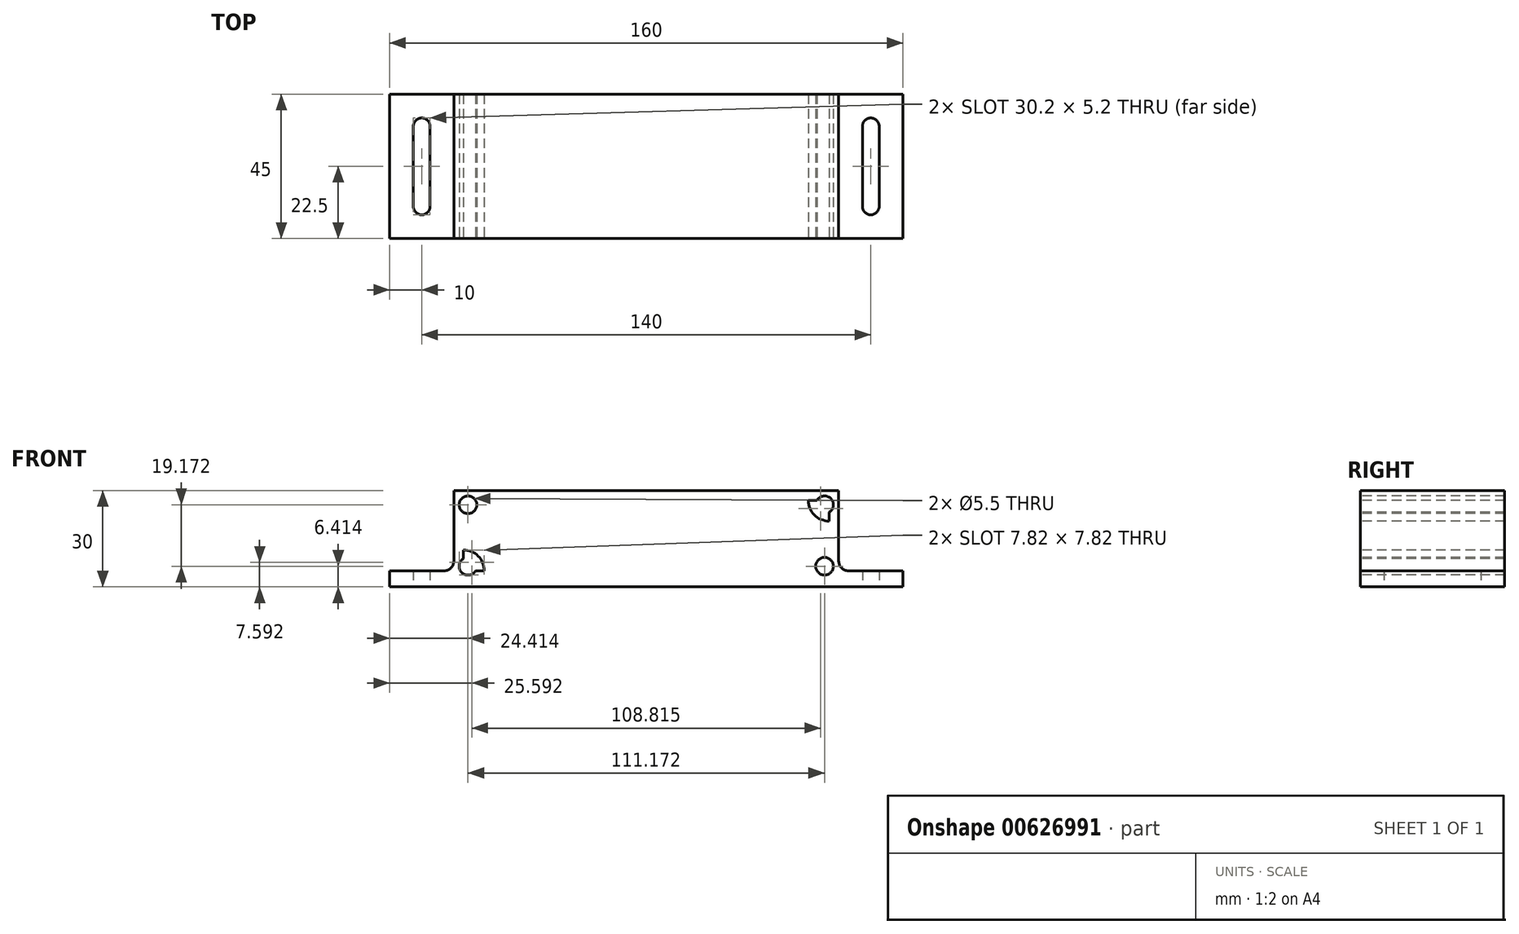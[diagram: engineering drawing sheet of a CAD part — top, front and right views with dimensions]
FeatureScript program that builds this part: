
annotation { "Feature Type Name" : "Feature", "Feature Type Description" : "" }
export const myFeature = defineFeature(function(context is Context, id is Id, definition is map)
    precondition{}
    {
        {
            var Q0;
            Q0=qCreatedBy(makeId("Front.planeOp"),FACE);
            var sketch = newSketch(context, id + "F0", { "sketchPlane" : qUnion([Q0])});
            skLineSegment(sketch, "E0", {"start": v(0, 0) * mm, "end": v(160, 0) * mm});
            skLineSegment(sketch, "E1", {"start": v(160, 0) * mm, "end": v(160, 5) * mm});
            skLineSegment(sketch, "E2", {"start": v(160, 5) * mm, "end": v(140, 5) * mm});
            skLineSegment(sketch, "E3", {"start": v(140, 5) * mm, "end": v(140, 30) * mm});
            skLineSegment(sketch, "E4", {"start": v(140, 30) * mm, "end": v(20, 30) * mm});
            skLineSegment(sketch, "E5", {"start": v(20, 30) * mm, "end": v(20, 5) * mm});
            skLineSegment(sketch, "E6", {"start": v(20, 5) * mm, "end": v(0, 5) * mm});
            skLineSegment(sketch, "E7", {"start": v(0, 5) * mm, "end": v(0, 0) * mm});
            skSolve(sketch);
        }
        {
            var Q0;
            Q0=qSketchRegion(id+"F0",true);
            extrude(context, id + "F1", {"entities" : qUnion([Q0]), "depth" : 45 * mm, "offsetDistance" : 25.4 * mm});
        }
        {
            var Q0;
            Q0=makeQuery(id+"F1.opExtrude","CAP_FACE",FACE,{"disambiguationData":[OSD([sQuery(id+"F0.wireOp",EDGE,"E0"),sQuery(id+"F0.wireOp",EDGE,"E1"),sQuery(id+"F0.wireOp",EDGE,"E2"),sQuery(id+"F0.wireOp",EDGE,"E3"),sQuery(id+"F0.wireOp",EDGE,"E4"),sQuery(id+"F0.wireOp",EDGE,"E5"),sQuery(id+"F0.wireOp",EDGE,"E6"),sQuery(id+"F0.wireOp",EDGE,"E7")])],"isStart":false});
            var sketch = newSketch(context, id + "F2", { "sketchPlane" : qUnion([Q0])});
            skLineSegment(sketch, "E8.bottom", {"start": v(23, 27) * mm, "end": v(137, 27) * mm});
            skLineSegment(sketch, "E8.top", {"start": v(23, 5) * mm, "end": v(137, 5) * mm});
            skLineSegment(sketch, "E8.left", {"start": v(23, 27) * mm, "end": v(23, 5) * mm});
            skLineSegment(sketch, "E8.right", {"start": v(137, 27) * mm, "end": v(137, 5) * mm});
            skSolve(sketch);
        }
        {
            var Q0;
            Q0=qSketchRegion(id+"F2",true);
            extrude(context, id + "F3", {"entities" : qUnion([Q0]), "operationType" : NewBodyOperationType.REMOVE, "oppositeDirection" : true, "depth" : 50 * mm, "offsetDistance" : 25.4 * mm});
        }
        {
            var Q0;
            Q0=makeQuery(id+"F1.opExtrude","CAP_FACE",FACE,{"disambiguationData":[OSD([sQuery(id+"F0.wireOp",EDGE,"E0"),sQuery(id+"F0.wireOp",EDGE,"E1"),sQuery(id+"F0.wireOp",EDGE,"E2"),sQuery(id+"F0.wireOp",EDGE,"E3"),sQuery(id+"F0.wireOp",EDGE,"E4"),sQuery(id+"F0.wireOp",EDGE,"E5"),sQuery(id+"F0.wireOp",EDGE,"E6"),sQuery(id+"F0.wireOp",EDGE,"E7")])],"isStart":false});
            var sketch = newSketch(context, id + "F4", { "sketchPlane" : qUnion([Q0])});
            skLineSegment(sketch, "E9", {"start": v(80, 5) * mm, "end": v(80, 27) * mm, "construction": true});
            skArc(sketch, "E10", {"start": v(23, 20.5) * mm, "mid": v(27.6, 22.4) * mm, "end": v(29.5, 27) * mm});
            skArc(sketch, "E11.MirrorCS", {"start": v(137, 20.5) * mm, "mid": v(132.4, 22.4) * mm, "end": v(130.5, 27) * mm});
            skLineSegment(sketch, "E12", {"start": v(23, 16) * mm, "end": v(137, 16) * mm, "construction": true});
            skArc(sketch, "E13.MirrorCS", {"start": v(23, 11.5) * mm, "mid": v(27.6, 9.6) * mm, "end": v(29.5, 5) * mm});
            skArc(sketch, "E14.MirrorCS", {"start": v(137, 11.5) * mm, "mid": v(132.4, 9.6) * mm, "end": v(130.5, 5) * mm});
            skSolve(sketch);
        }
        {
            var Q0;
            {var subQ0=sQuery(id+"F4.wireOp",EDGE,"E13.MirrorCS");Q0=makeQuery(id+"F4.imprint","IMPRINT",FACE,{"disambiguationData":[TD([[makeQuery(id+"F4.imprint","IMPRINT",EDGE,{"derivedFrom":subQ0}),-1.0]])]});}
            var Q1;
            {var subQ0=sQuery(id+"F4.wireOp",EDGE,"E10");Q1=makeQuery(id+"F4.imprint","IMPRINT",FACE,{"disambiguationData":[TD([[makeQuery(id+"F4.imprint","IMPRINT",EDGE,{"derivedFrom":subQ0}),1.0]])]});}
            var Q2;
            {var subQ0=sQuery(id+"F4.wireOp",EDGE,"E11.MirrorCS");Q2=makeQuery(id+"F4.imprint","IMPRINT",FACE,{"disambiguationData":[TD([[makeQuery(id+"F4.imprint","IMPRINT",EDGE,{"derivedFrom":subQ0}),-1.0]])]});}
            var Q3;
            {var subQ0=sQuery(id+"F4.wireOp",EDGE,"E14.MirrorCS");Q3=makeQuery(id+"F4.imprint","IMPRINT",FACE,{"disambiguationData":[TD([[makeQuery(id+"F4.imprint","IMPRINT",EDGE,{"derivedFrom":subQ0}),1.0]])]});}
            var Q4;
            Q4=makeQuery(id+"F1.opExtrude","CAP_FACE",FACE,{"disambiguationData":[OSD([sQuery(id+"F0.wireOp",EDGE,"E0"),sQuery(id+"F0.wireOp",EDGE,"E1"),sQuery(id+"F0.wireOp",EDGE,"E2"),sQuery(id+"F0.wireOp",EDGE,"E3"),sQuery(id+"F0.wireOp",EDGE,"E4"),sQuery(id+"F0.wireOp",EDGE,"E5"),sQuery(id+"F0.wireOp",EDGE,"E6"),sQuery(id+"F0.wireOp",EDGE,"E7")])],"isStart":true});
            extrude(context, id + "F5", {"entities" : qUnion([Q0, Q1, Q2, Q3]), "operationType" : NewBodyOperationType.ADD, "endBound" : BoundingType.UP_TO_SURFACE, "oppositeDirection" : true, "depth" : 5 * mm, "endBoundEntityFace" : qUnion([Q4]), "offsetDistance" : 25.4 * mm});
        }
        {
            var Q0;
            Q0=makeQuery(id+"F1.opExtrude","SWEPT_EDGE",EDGE,{"disambiguationData":[OSD([sQuery(id+"F0.wireOp",EDGE,"E2"),sQuery(id+"F0.wireOp",EDGE,"E3")])]});
            var Q1;
            Q1=makeQuery(id+"F1.opExtrude","SWEPT_EDGE",EDGE,{"disambiguationData":[OSD([sQuery(id+"F0.wireOp",EDGE,"E5"),sQuery(id+"F0.wireOp",EDGE,"E6")])]});
            fillet(context, id + "F6", {"entities" : qUnion([Q0, Q1]), "radius" : 3 * mm, "tangentPropagation" : true, "allowEdgeOverflow" : false});
        }
        {
            var Q0;
            Q0=makeQuery(id+"F1.opExtrude","SWEPT_FACE",FACE,{"disambiguationData":[OSD([sQuery(id+"F0.wireOp",EDGE,"E0")])]});
            var sketch = newSketch(context, id + "F7", { "sketchPlane" : qUnion([Q0])});
            skLineSegment(sketch, "E15", {"start": v(80, 45) * mm, "end": v(80, 0) * mm, "construction": true});
            skLineSegment(sketch, "E16", {"start": v(10, 35) * mm, "end": v(10, 10) * mm});
            skArc(sketch, "E17.0.startCap", {"start": v(7.4, 35) * mm, "mid": v(10, 37.6) * mm, "end": v(12.6, 35) * mm});
            skArc(sketch, "E17.0.endCap", {"start": v(12.6, 10) * mm, "mid": v(10, 7.4) * mm, "end": v(7.4, 10) * mm});
            skLineSegment(sketch, "E17.0.left", {"start": v(12.6, 35) * mm, "end": v(12.6, 10) * mm});
            skLineSegment(sketch, "E17.0.right", {"start": v(7.4, 35) * mm, "end": v(7.4, 10) * mm});
            skLineSegment(sketch, "E18.MirrorCS", {"start": v(147.4, 35) * mm, "end": v(147.4, 10) * mm});
            skArc(sketch, "E19.MirrorCS", {"start": v(152.6, 35) * mm, "mid": v(150, 37.6) * mm, "end": v(147.4, 35) * mm});
            skLineSegment(sketch, "E20.MirrorCS", {"start": v(152.6, 35) * mm, "end": v(152.6, 10) * mm});
            skLineSegment(sketch, "E21.MirrorCS", {"start": v(150, 35) * mm, "end": v(150, 10) * mm});
            skArc(sketch, "E22.MirrorCS", {"start": v(147.4, 10) * mm, "mid": v(150, 7.4) * mm, "end": v(152.6, 10) * mm});
            skSolve(sketch);
        }
        {
            var Q0;
            Q0=qSketchRegion(id+"F7",true);
            extrude(context, id + "F8", {"entities" : qUnion([Q0]), "operationType" : NewBodyOperationType.REMOVE, "endBound" : BoundingType.UP_TO_NEXT, "oppositeDirection" : true, "depth" : 25.4 * mm, "offsetDistance" : 25.4 * mm});
        }
        {
            var Q0;
            {var subQ0=sQuery(id+"F2.wireOp",EDGE,"E8.right");var subQ1=sQuery(id+"F2.wireOp",EDGE,"E8.top");var subQ2=sQuery(id+"F2.wireOp",EDGE,"E8.left");var subQ3=sQuery(id+"F2.wireOp",EDGE,"E8.bottom");Q0=makeQuery(id+"FeQkn0KcMcVrZGf_5.boolean.opBoolean","MERGE",FACE,{"derivedFrom":[makeQuery(id+"F5.opExtrude","CAP_FACE",FACE,{"disambiguationData":[OSD([subQ3,subQ2,sQuery(id+"F4.wireOp",EDGE,"E10")])],"isStart":true}),makeQuery(id+"F5.opExtrude","CAP_FACE",FACE,{"disambiguationData":[OSD([subQ3,subQ0,sQuery(id+"F4.wireOp",EDGE,"E11.MirrorCS")])],"isStart":true}),makeQuery(id+"F5.opExtrude","CAP_FACE",FACE,{"disambiguationData":[OSD([subQ1,subQ2,sQuery(id+"F4.wireOp",EDGE,"E13.MirrorCS")])],"isStart":true}),makeQuery(id+"F5.opExtrude","CAP_FACE",FACE,{"disambiguationData":[OSD([subQ1,subQ0,sQuery(id+"F4.wireOp",EDGE,"E14.MirrorCS")])],"isStart":true}),makeQuery(id+"F1.opExtrude","CAP_FACE",FACE,{"disambiguationData":[OSD([sQuery(id+"F0.wireOp",EDGE,"E0"),sQuery(id+"F0.wireOp",EDGE,"E1"),sQuery(id+"F0.wireOp",EDGE,"E2"),sQuery(id+"F0.wireOp",EDGE,"E3"),sQuery(id+"F0.wireOp",EDGE,"E4"),sQuery(id+"F0.wireOp",EDGE,"E5"),sQuery(id+"F0.wireOp",EDGE,"E6"),sQuery(id+"F0.wireOp",EDGE,"E7")])],"isStart":false})]});}
            var sketch = newSketch(context, id + "F9", { "sketchPlane" : qUnion([Q0])});
            skLineSegment(sketch, "E23", {"start": v(27.6, 22.4) * mm, "end": v(20, 30) * mm, "construction": true});
            skPoint(sketch, "E24", {"position": v(24.41, 25.59) * mm});
            skLineSegment(sketch, "E25", {"start": v(80, 30) * mm, "end": v(80, 0) * mm, "construction": true});
            skPoint(sketch, "E26.MirrorP", {"position": v(135.59, 25.59) * mm});
            skLineSegment(sketch, "E27", {"start": v(23, 16) * mm, "end": v(137, 16) * mm, "construction": true});
            skPoint(sketch, "E28.MirrorP", {"position": v(135.59, 6.41) * mm});
            skPoint(sketch, "E29.MirrorP", {"position": v(24.41, 6.41) * mm});
            skSolve(sketch);
        }
        {
            var Q0;
            Q0=sQuery(id+"F9.wireOp",VERTEX,"E24");
            var Q1;
            Q1=sQuery(id+"F9.wireOp",VERTEX,"E29.MirrorP");
            var Q2;
            Q2=sQuery(id+"F9.wireOp",VERTEX,"E28.MirrorP");
            var Q3;
            Q3=sQuery(id+"F9.wireOp",VERTEX,"E26.MirrorP");
            var Q4;
            Q4=makeQuery(id+"F1.opExtrude","SWEPT_BODY",BODY,{"disambiguationData":[OSD([sQuery(id+"F0.wireOp",EDGE,"E0"),sQuery(id+"F0.wireOp",EDGE,"E1"),sQuery(id+"F0.wireOp",EDGE,"E2"),sQuery(id+"F0.wireOp",EDGE,"E3"),sQuery(id+"F0.wireOp",EDGE,"E4"),sQuery(id+"F0.wireOp",EDGE,"E5"),sQuery(id+"F0.wireOp",EDGE,"E6"),sQuery(id+"F0.wireOp",EDGE,"E7")])]});
            hole(context, id + "F10", {"style" : HoleStyle.SIMPLE, "endStyle" : HoleEndStyle.THROUGH, "holeDiameter" : 5.5 * mm, "majorDiameter" : 6.35 * mm, "isTappedThrough" : true, "tappedDepth" : 12.7 * mm, "tapClearance" : 3, "locations" : qUnion([Q0, Q1, Q2, Q3]), "scope" : qUnion([Q4])});
        }
    });
